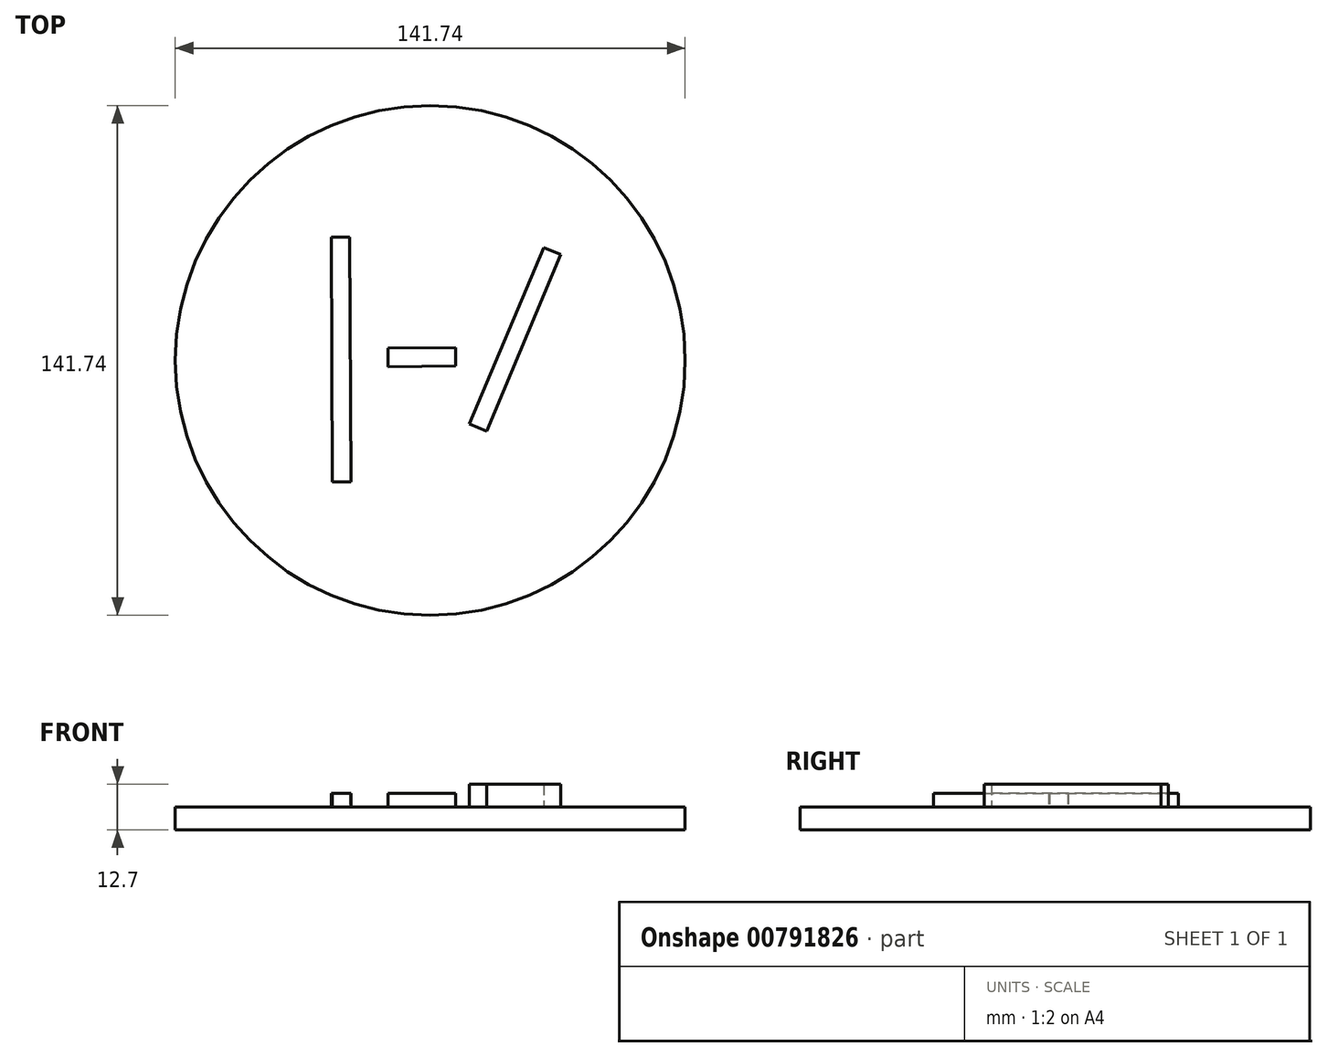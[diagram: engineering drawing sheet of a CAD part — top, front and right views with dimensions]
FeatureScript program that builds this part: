
annotation { "Feature Type Name" : "Feature", "Feature Type Description" : "" }
export const myFeature = defineFeature(function(context is Context, id is Id, definition is map)
    precondition{}
    {
        {
            var Q0;
            Q0=qCreatedBy(makeId("Top.planeOp"),FACE);
            var sketch = newSketch(context, id + "F0", { "sketchPlane" : qUnion([Q0])});
            skCircle(sketch, "E0", {"center": v(0, 0) * mm, "radius": 70.87 * mm});
            skLineSegment(sketch, "E1", {"start": v(-27.54, 34.27) * mm, "end": v(-22.41, 34.27) * mm});
            skLineSegment(sketch, "E2", {"start": v(-22.41, 34.27) * mm, "end": v(-22.01, -33.82) * mm});
            skLineSegment(sketch, "E3", {"start": v(-22.01, -33.82) * mm, "end": v(-27.2, -33.85) * mm});
            skLineSegment(sketch, "E4", {"start": v(-27.2, -33.85) * mm, "end": v(-27.54, 34.27) * mm});
            skLineSegment(sketch, "E5", {"start": v(7.04, 3.58) * mm, "end": v(7.04, -1.53) * mm});
            skLineSegment(sketch, "E6", {"start": v(7.04, -1.53) * mm, "end": v(-11.78, -1.8) * mm});
            skLineSegment(sketch, "E7", {"start": v(-11.78, -1.8) * mm, "end": v(-11.78, 3.47) * mm});
            skLineSegment(sketch, "E8", {"start": v(-11.78, 3.47) * mm, "end": v(7.04, 3.58) * mm});
            skLineSegment(sketch, "E9", {"start": v(31.55, 31.4) * mm, "end": v(36.25, 29.43) * mm});
            skLineSegment(sketch, "E10", {"start": v(36.25, 29.43) * mm, "end": v(15.74, -19.72) * mm});
            skLineSegment(sketch, "E11", {"start": v(15.74, -19.72) * mm, "end": v(10.87, -17.69) * mm});
            skLineSegment(sketch, "E12", {"start": v(10.87, -17.69) * mm, "end": v(31.55, 31.4) * mm});
            skSolve(sketch);
        }
        {
            var Q0;
            Q0 = qSketchRegion(id + "F0", true);
            extrude(context, id + "F1", {"entities" : qUnion([Q0]), "depth" : 6.35 * mm, "offsetDistance" : 25.4 * mm});
        }
        {
            var Q0;
            Q0=makeQuery(id+"F0.imprint","IMPRINT",FACE,{"disambiguationData":[TD([[makeQuery(id+"F0.imprint","IMPRINT",EDGE,{"derivedFrom":sQuery(id+"F0.wireOp",EDGE,"E1")}),-1.0]])]});
            var Q1;
            Q1=makeQuery(id+"F0.imprint","IMPRINT",FACE,{"disambiguationData":[TD([[makeQuery(id+"F0.imprint","IMPRINT",EDGE,{"derivedFrom":sQuery(id+"F0.wireOp",EDGE,"E5")}),-1.0]])]});
            extrude(context, id + "F2", {"entities" : qUnion([Q0, Q1]), "operationType" : NewBodyOperationType.ADD, "depth" : 10.16 * mm, "offsetDistance" : 25.4 * mm});
        }
        {
            var Q0;
            Q0=makeQuery(id+"F0.imprint","IMPRINT",FACE,{"disambiguationData":[TD([[makeQuery(id+"F0.imprint","IMPRINT",EDGE,{"derivedFrom":sQuery(id+"F0.wireOp",EDGE,"E9")}),-1.0]])]});
            extrude(context, id + "F3", {"entities" : qUnion([Q0]), "operationType" : NewBodyOperationType.ADD, "depth" : 12.7 * mm, "offsetDistance" : 25.4 * mm});
        }
    });
